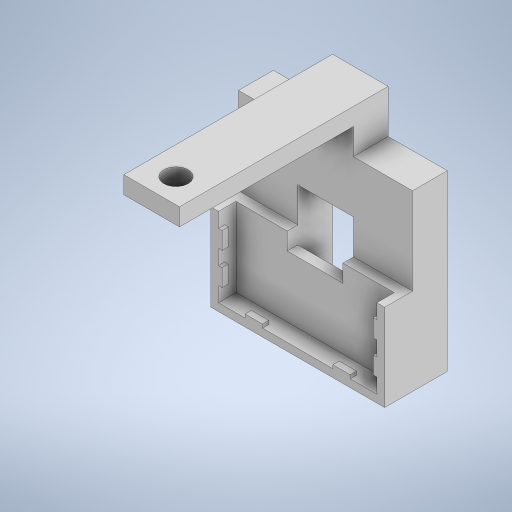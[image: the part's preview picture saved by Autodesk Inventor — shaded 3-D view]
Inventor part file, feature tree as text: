
AUTODESK INVENTOR PART (.ipt)
format: ipt  version: 2023 (Build 270158000, 158)  size: 363,520 bytes
history: native  units: in
note: dims shown in document units (in); Inventor stores cm internally (conversion verified against a paired STEP export)
features: extrude x8, sketch x8
ambient origin geometry x8: Origin, YZ Plane, XZ Plane, XY Plane, X Axis, Y Axis, Z Axis, Center Point
bodies: Solid1 (feature_tree)
feature tree (16):
  extrude  "Extrusion1"  TaperAngle=0.0deg  [1 undecoded]
  extrude  "Extrusion2"  Depth=0.1181in TaperAngle=0.0deg
  extrude  "Extrusion3"  TaperAngle=0.0deg  [1 undecoded]
  extrude  "Extrusion4"  Depth=0.1969in TaperAngle=0.0deg
  extrude  "Extrusion5"  Depth=0.1969in
  extrude  "Extrusion6"  Depth=0.0394in TaperAngle=0.0deg
  extrude  "Extrusion7"  Depth=0.3937in TaperAngle=0.0deg
  extrude  "Extrusion15"  Depth=0.1969in
  sketch  "Sketch1"  dims[d0=1.9685in d1=0.0in]
  sketch  "Sketch2"  dims[d2=0.9843in d3=0.1181in d4=0.0in]
  sketch  "Sketch3"  dims[d5=1.7913in d6=0.0in]
  sketch  "Sketch4"  dims[d7=0.8071in d8=0.1969in d9=0.0in]
  sketch  "Sketch5"  dims[d10=0.1969in d11=0.1969in]
  sketch  "Sketch6"  dims[d12=0.0394in d13=0.0in d14=0.0394in d15=0.0in]
  sketch  "Sketch7"  dims[d22=0.0394in d23=0.0in d26=0.3937in d27=0.0in]
  sketch  "Sketch18"  dims[d28=0.0709in d31=0.1969in d32=0.0709in d33=0.1969in d34=0.0709in d35=0.6299in d36=0.1969in d37=0.0in d38=0.0in d41=0.6693in d42=1.9685in d43=0.6693in d44=1.9685in d47=0.6299in d49=0.0in d86=1.9685in d87=0.2756in d88=0.2756in d89=0.1969in d90=0.0in d39=0.0197in d40=0.0344in]
note: 2 required parameter values undecoded (feature->parameter linkage not recoverable at this tier; creation-order binding heuristic only, values carry confidence <= 0.55)
